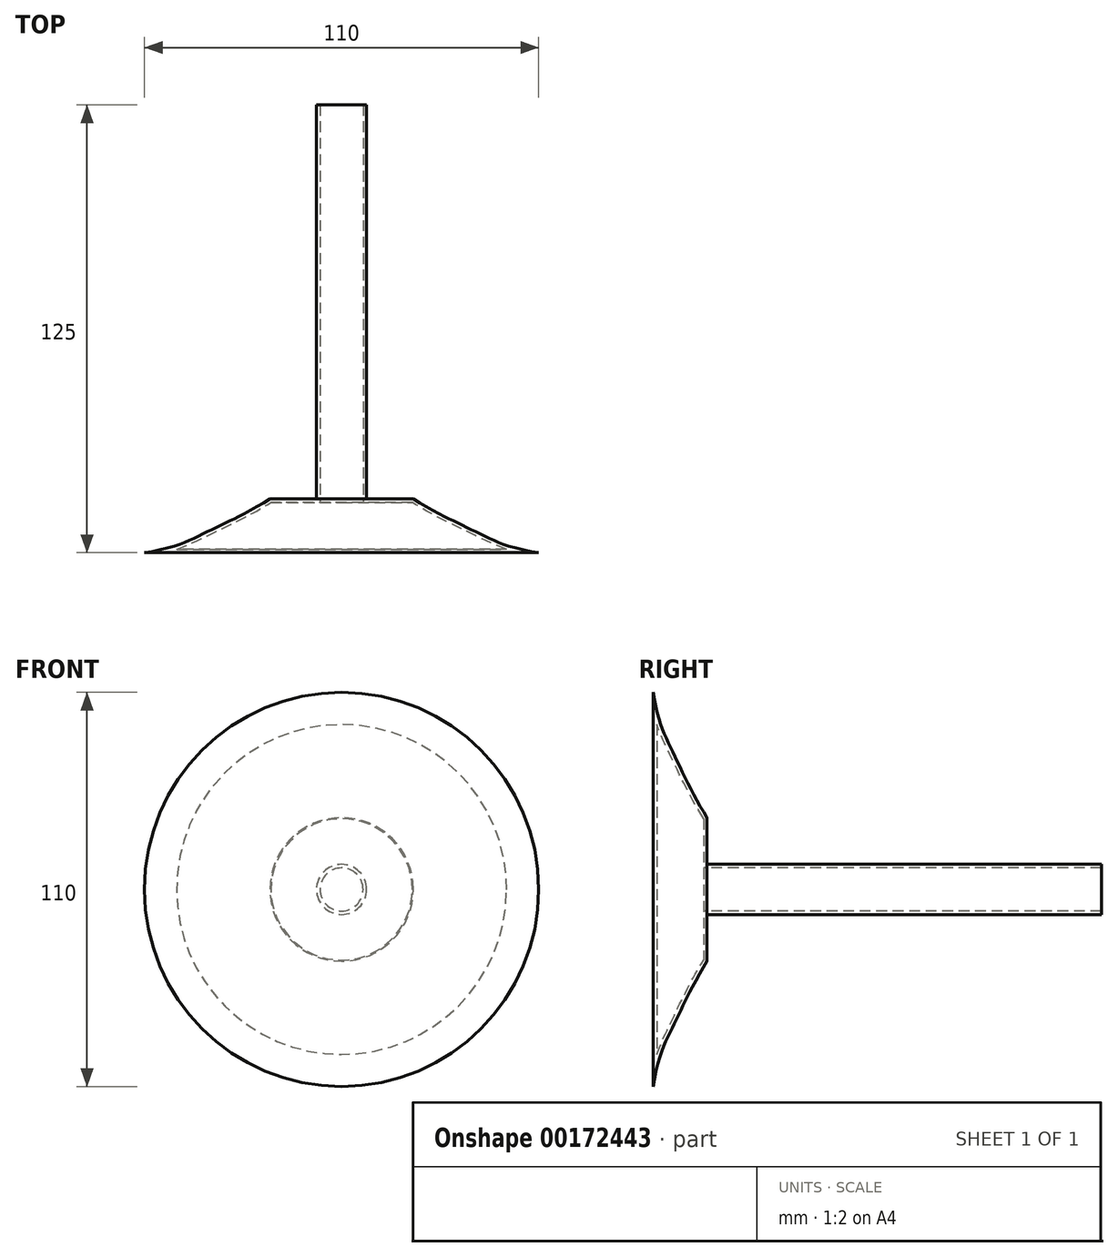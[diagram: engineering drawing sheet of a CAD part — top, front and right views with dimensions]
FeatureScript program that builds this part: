
annotation { "Feature Type Name" : "Feature", "Feature Type Description" : "" }
export const myFeature = defineFeature(function(context is Context, id is Id, definition is map)
    precondition{}
    {
        {
            var Q0;
            Q0=qCreatedBy(makeId("Top.planeOp"),FACE);
            var sketch = newSketch(context, id + "F0", { "sketchPlane" : qUnion([Q0])});
            skLineSegment(sketch, "E0", {"start": v(0, 15) * mm, "end": v(20, 15) * mm});
            skLineSegment(sketch, "E1", {"start": v(0, 15) * mm, "end": v(0, 0) * mm});
            skLineSegment(sketch, "E2", {"start": v(0, 0) * mm, "end": v(55, 0) * mm});
            skFitSpline(sketch, "E3", {"points": [v(20, 15) * mm, v(38.39, 5.4) * mm, v(55, 0) * mm], "startDerivative": vector(36.87, -22.86) * mm, "endDerivative": vector(51.27, -7.45) * mm});
            skSolve(sketch);
        }
        {
            var Q0;
            Q0=makeQuery(id+"F0.imprint","IMPRINT",FACE,{"disambiguationData":[TD([[makeQuery(id+"F0.imprint","IMPRINT",EDGE,{"derivedFrom":sQuery(id+"F0.wireOp",EDGE,"E0")}),-1.0]])]});
            var Q1;
            Q1=sQuery(id+"F0.wireOp",EDGE,"E1");
            revolve(context, id + "F1", {"entities" : qUnion([Q0]), "axis" : qUnion([Q1]), "revolveType" : RevolveType.FULL});
        }
        {
            var Q0;
            Q0=makeQuery(id+"F1.opRevolve","SWEPT_FACE",FACE,{"disambiguationData":[OSD([sQuery(id+"F0.wireOp",EDGE,"E0")])]});
            var sketch = newSketch(context, id + "F2", { "sketchPlane" : qUnion([Q0])});
            skCircle(sketch, "E4", {"center": v(0, 0) * mm, "radius": 7 * mm});
            skSolve(sketch);
        }
        {
            var Q0;
            Q0 = qSketchRegion(id + "F2", true);
            extrude(context, id + "F3", {"entities" : qUnion([Q0]), "operationType" : NewBodyOperationType.ADD, "depth" : 110 * mm});
        }
        {
            var Q0;
            Q0=makeQuery(id+"F3.opExtrude","CAP_FACE",FACE,{"disambiguationData":[OSD([sQuery(id+"F2.wireOp",EDGE,"E4")])],"isStart":false});
            shell(context, id + "F4", {"entities" : qUnion([Q0]), "thickness" : 1 * mm});
        }
    });
